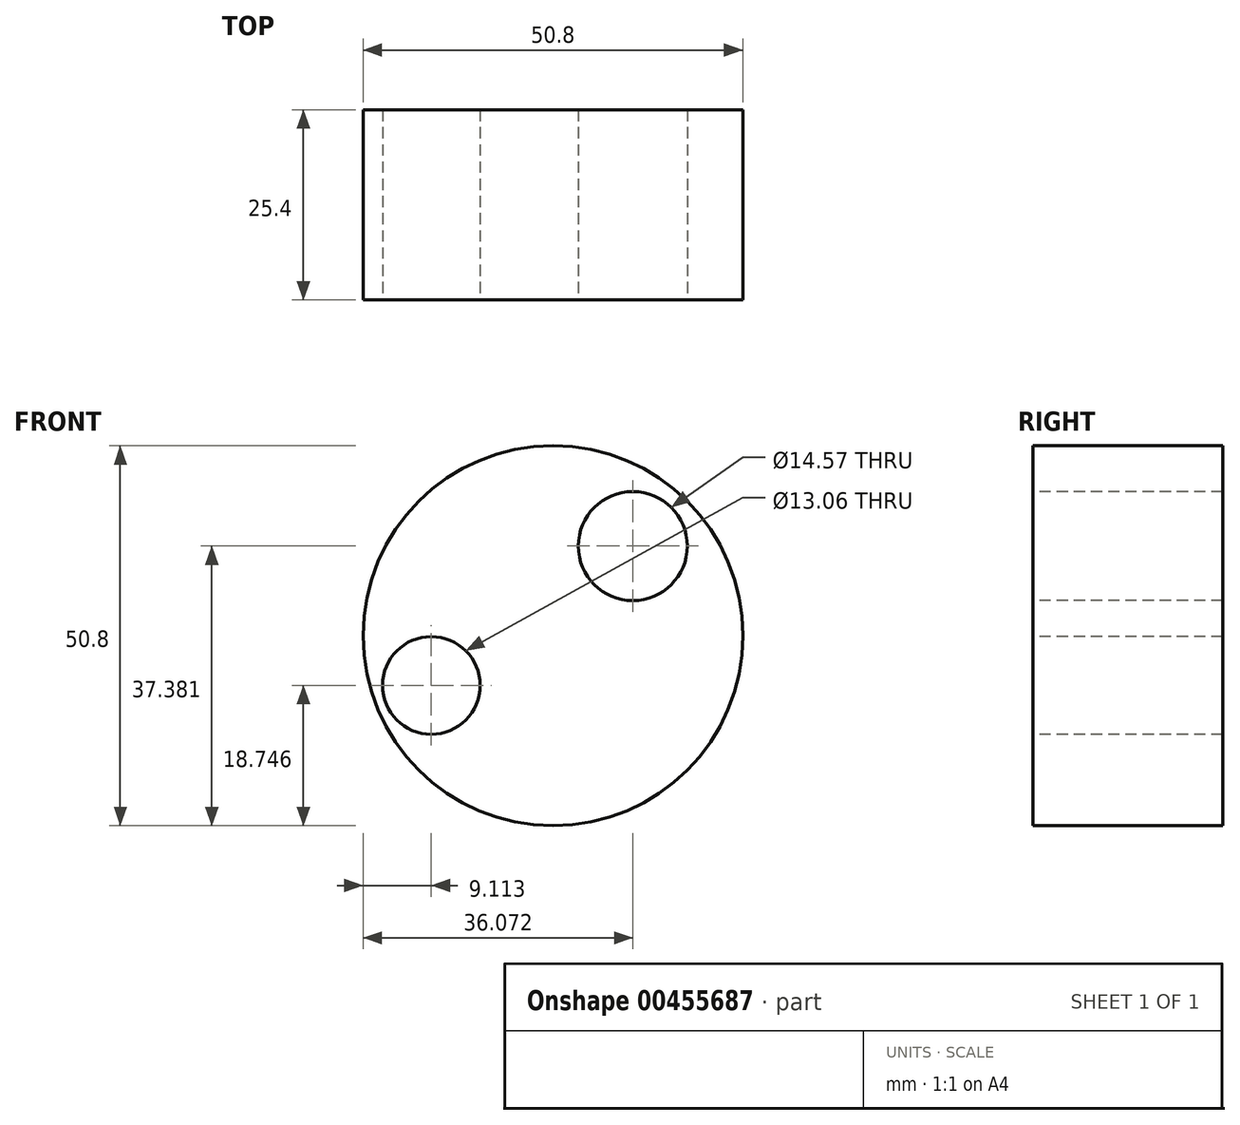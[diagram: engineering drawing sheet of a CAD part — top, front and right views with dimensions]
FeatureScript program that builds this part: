
annotation { "Feature Type Name" : "Feature", "Feature Type Description" : "" }
export const myFeature = defineFeature(function(context is Context, id is Id, definition is map)
    precondition{}
    {
        {
            var Q0;
            Q0=qCreatedBy(makeId("Front.planeOp"),FACE);
            var sketch = newSketch(context, id + "F0", { "sketchPlane" : qUnion([Q0])});
            skCircle(sketch, "E0", {"center": v(0, 0) * mm, "radius": 25.4 * mm});
            skSolve(sketch);
        }
        {
            var Q0;
            Q0=makeQuery(id+"F0.imprint","IMPRINT",FACE,{"disambiguationData":[TD([[makeQuery(id+"F0.imprint","IMPRINT",EDGE,{"derivedFrom":sQuery(id+"F0.wireOp",EDGE,"E0")}),1.0]])]});
            extrude(context, id + "F1", {"entities" : qUnion([Q0]), "depth" : 25.4 * mm});
        }
        {
            var Q0;
            Q0=makeQuery(id+"F1.opExtrude","CAP_FACE",FACE,{"disambiguationData":[OSD([sQuery(id+"F0.wireOp",EDGE,"E0")])],"isStart":false});
            var sketch = newSketch(context, id + "F2", { "sketchPlane" : qUnion([Q0])});
            skCircle(sketch, "E1", {"center": v(-14.77, 8.55) * mm, "radius": 4.48 * mm});
            skCircle(sketch, "E2", {"center": v(10.67, 11.98) * mm, "radius": 7.28 * mm});
            skCircle(sketch, "E3", {"center": v(-16.29, -6.65) * mm, "radius": 6.53 * mm});
            skSolve(sketch);
        }
        {
            var Q0;
            Q0=makeQuery(id+"F2.imprint","IMPRINT",FACE,{"disambiguationData":[TD([[makeQuery(id+"F2.imprint","IMPRINT",EDGE,{"derivedFrom":sQuery(id+"F2.wireOp",EDGE,"E3")}),1.0]])]});
            var Q1;
            Q1=makeQuery(id+"F2.imprint","IMPRINT",FACE,{"disambiguationData":[TD([[makeQuery(id+"F2.imprint","IMPRINT",EDGE,{"derivedFrom":sQuery(id+"F2.wireOp",EDGE,"E2")}),1.0]])]});
            extrude(context, id + "F3", {"entities" : qUnion([Q0, Q1]), "operationType" : NewBodyOperationType.REMOVE, "oppositeDirection" : true, "depth" : 25.4 * mm});
        }
    });
